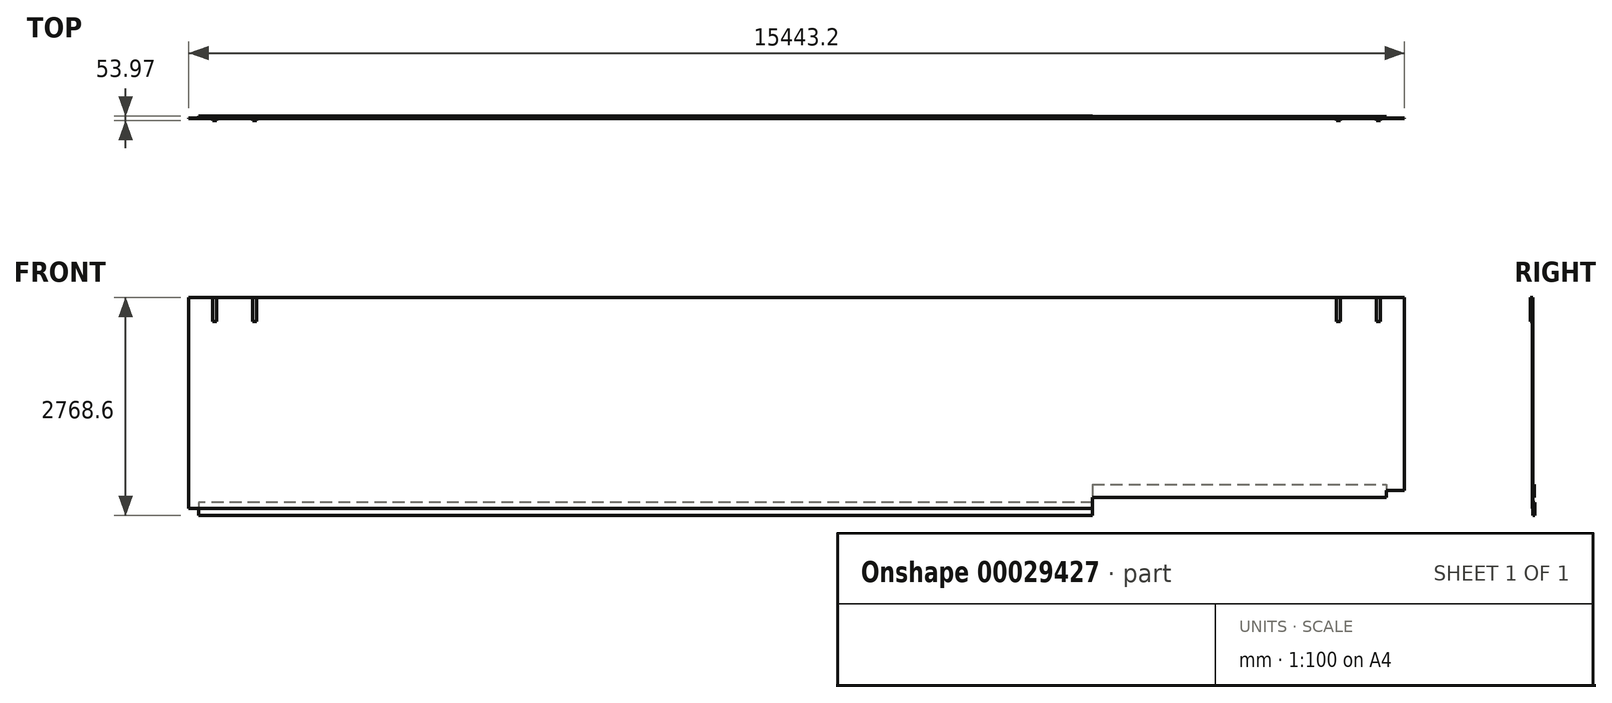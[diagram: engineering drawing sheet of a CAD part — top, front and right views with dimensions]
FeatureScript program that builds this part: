
annotation { "Feature Type Name" : "Feature", "Feature Type Description" : "" }
export const myFeature = defineFeature(function(context is Context, id is Id, definition is map)
    precondition{}
    {
        {
            var Q0;
            Q0=qCreatedBy(makeId("Front.planeOp"),FACE);
            var sketch = newSketch(context, id + "F0", { "sketchPlane" : qUnion([Q0])});
            skLineSegment(sketch, "E0.bottom", {"start": v(0, 0) * mm, "end": v(11480.8, 0) * mm});
            skLineSegment(sketch, "E0.top", {"start": v(0, 2679.7) * mm, "end": v(15443.2, 2679.7) * mm});
            skLineSegment(sketch, "E0.left", {"start": v(0, 0) * mm, "end": v(0, 2679.7) * mm});
            skLineSegment(sketch, "E0.right", {"start": v(15443.2, 228.6) * mm, "end": v(15443.2, 2679.7) * mm});
            skLineSegment(sketch, "E1", {"start": v(15443.2, 228.6) * mm, "end": v(11480.8, 228.6) * mm});
            skLineSegment(sketch, "E2", {"start": v(11480.8, 228.6) * mm, "end": v(11480.8, 0) * mm});
            skSolve(sketch);
        }
        {
            var Q0;
            Q0 = qSketchRegion(id + "F0", true);
            extrude(context, id + "F1", {"entities" : qUnion([Q0]), "depth" : 3.17 * mm});
        }
        {
            var Q0;
            Q0=makeQuery(id+"F1.opExtrude","CAP_FACE",FACE,{"disambiguationData":[OSD([sQuery(id+"F0.wireOp",EDGE,"E0.bottom"),sQuery(id+"F0.wireOp",EDGE,"E0.top"),sQuery(id+"F0.wireOp",EDGE,"E0.left"),sQuery(id+"F0.wireOp",EDGE,"E0.right"),sQuery(id+"F0.wireOp",EDGE,"E1"),sQuery(id+"F0.wireOp",EDGE,"E2")])],"isStart":true});
            var sketch = newSketch(context, id + "F2", { "sketchPlane" : qUnion([Q0])});
            skLineSegment(sketch, "E3.bottom", {"start": v(-11480.8, 76.2) * mm, "end": v(-127, 76.2) * mm});
            skLineSegment(sketch, "E3.top", {"start": v(-11480.8, -88.9) * mm, "end": v(-127, -88.9) * mm});
            skLineSegment(sketch, "E3.left", {"start": v(-11480.8, 76.2) * mm, "end": v(-11480.8, -88.9) * mm});
            skLineSegment(sketch, "E3.right", {"start": v(-127, 76.2) * mm, "end": v(-127, -88.9) * mm});
            skSolve(sketch);
        }
        {
            var Q0;
            Q0 = qSketchRegion(id + "F2", true);
            extrude(context, id + "F3", {"entities" : qUnion([Q0]), "operationType" : NewBodyOperationType.ADD, "depth" : 25.4 * mm});
        }
        {
            var Q0;
            Q0=makeQuery(id+"F1.opExtrude","CAP_FACE",FACE,{"disambiguationData":[OSD([sQuery(id+"F0.wireOp",EDGE,"E0.bottom"),sQuery(id+"F0.wireOp",EDGE,"E0.top"),sQuery(id+"F0.wireOp",EDGE,"E0.left"),sQuery(id+"F0.wireOp",EDGE,"E0.right"),sQuery(id+"F0.wireOp",EDGE,"E1"),sQuery(id+"F0.wireOp",EDGE,"E2")])],"isStart":false});
            var sketch = newSketch(context, id + "F4", { "sketchPlane" : qUnion([Q0])});
            skLineSegment(sketch, "E4.bottom", {"start": v(11480.8, 304.8) * mm, "end": v(15214.6, 304.8) * mm});
            skLineSegment(sketch, "E4.top", {"start": v(11480.8, 139.7) * mm, "end": v(15214.6, 139.7) * mm});
            skLineSegment(sketch, "E4.left", {"start": v(11480.8, 304.8) * mm, "end": v(11480.8, 139.7) * mm});
            skLineSegment(sketch, "E4.right", {"start": v(15214.6, 304.8) * mm, "end": v(15214.6, 139.7) * mm});
            skSolve(sketch);
        }
        {
            var Q0;
            Q0 = qSketchRegion(id + "F4", true);
            extrude(context, id + "F5", {"entities" : qUnion([Q0]), "operationType" : NewBodyOperationType.ADD, "oppositeDirection" : true, "depth" : 25.4 * mm});
        }
        {
            var Q0;
            Q0=makeQuery(id+"F5.boolean.opBoolean","MERGE",FACE,{"derivedFrom":[makeQuery(id+"F1.opExtrude","CAP_FACE",FACE,{"disambiguationData":[OSD([sQuery(id+"F0.wireOp",EDGE,"E0.bottom"),sQuery(id+"F0.wireOp",EDGE,"E0.top"),sQuery(id+"F0.wireOp",EDGE,"E0.left"),sQuery(id+"F0.wireOp",EDGE,"E0.right"),sQuery(id+"F0.wireOp",EDGE,"E1"),sQuery(id+"F0.wireOp",EDGE,"E2")])],"isStart":false}),makeQuery(id+"F5.opExtrude","CAP_FACE",FACE,{"disambiguationData":[OSD([sQuery(id+"F4.wireOp",EDGE,"E4.bottom"),sQuery(id+"F4.wireOp",EDGE,"E4.top"),sQuery(id+"F4.wireOp",EDGE,"E4.left"),sQuery(id+"F4.wireOp",EDGE,"E4.right")])],"isStart":true})]});
            var sketch = newSketch(context, id + "F6", { "sketchPlane" : qUnion([Q0])});
            skLineSegment(sketch, "E5.bottom", {"start": v(304.8, 2679.7) * mm, "end": v(355.6, 2679.7) * mm});
            skLineSegment(sketch, "E5.top", {"start": v(304.8, 2374.9) * mm, "end": v(355.6, 2374.9) * mm});
            skLineSegment(sketch, "E5.left", {"start": v(304.8, 2679.7) * mm, "end": v(304.8, 2374.9) * mm});
            skLineSegment(sketch, "E5.right", {"start": v(355.6, 2679.7) * mm, "end": v(355.6, 2374.9) * mm});
            skLineSegment(sketch, "E6.bottom", {"start": v(812.8, 2679.7) * mm, "end": v(863.6, 2679.7) * mm});
            skLineSegment(sketch, "E6.top", {"start": v(812.8, 2374.9) * mm, "end": v(863.6, 2374.9) * mm});
            skLineSegment(sketch, "E6.left", {"start": v(812.8, 2679.7) * mm, "end": v(812.8, 2374.9) * mm});
            skLineSegment(sketch, "E6.right", {"start": v(863.6, 2679.7) * mm, "end": v(863.6, 2374.9) * mm});
            skLineSegment(sketch, "E7.bottom", {"start": v(15087.6, 2679.7) * mm, "end": v(15138.4, 2679.7) * mm});
            skLineSegment(sketch, "E7.top", {"start": v(15087.6, 2374.9) * mm, "end": v(15138.4, 2374.9) * mm});
            skLineSegment(sketch, "E7.left", {"start": v(15087.6, 2679.7) * mm, "end": v(15087.6, 2374.9) * mm});
            skLineSegment(sketch, "E7.right", {"start": v(15138.4, 2679.7) * mm, "end": v(15138.4, 2374.9) * mm});
            skLineSegment(sketch, "E8.bottom", {"start": v(14579.6, 2679.7) * mm, "end": v(14630.4, 2679.7) * mm});
            skLineSegment(sketch, "E8.top", {"start": v(14579.6, 2374.9) * mm, "end": v(14630.4, 2374.9) * mm});
            skLineSegment(sketch, "E8.left", {"start": v(14579.6, 2679.7) * mm, "end": v(14579.6, 2374.9) * mm});
            skLineSegment(sketch, "E8.right", {"start": v(14630.4, 2679.7) * mm, "end": v(14630.4, 2374.9) * mm});
            skSolve(sketch);
        }
        {
            var Q0;
            Q0 = qSketchRegion(id + "F6", true);
            extrude(context, id + "F7", {"entities" : qUnion([Q0]), "operationType" : NewBodyOperationType.ADD, "depth" : 25.4 * mm});
        }
    });
